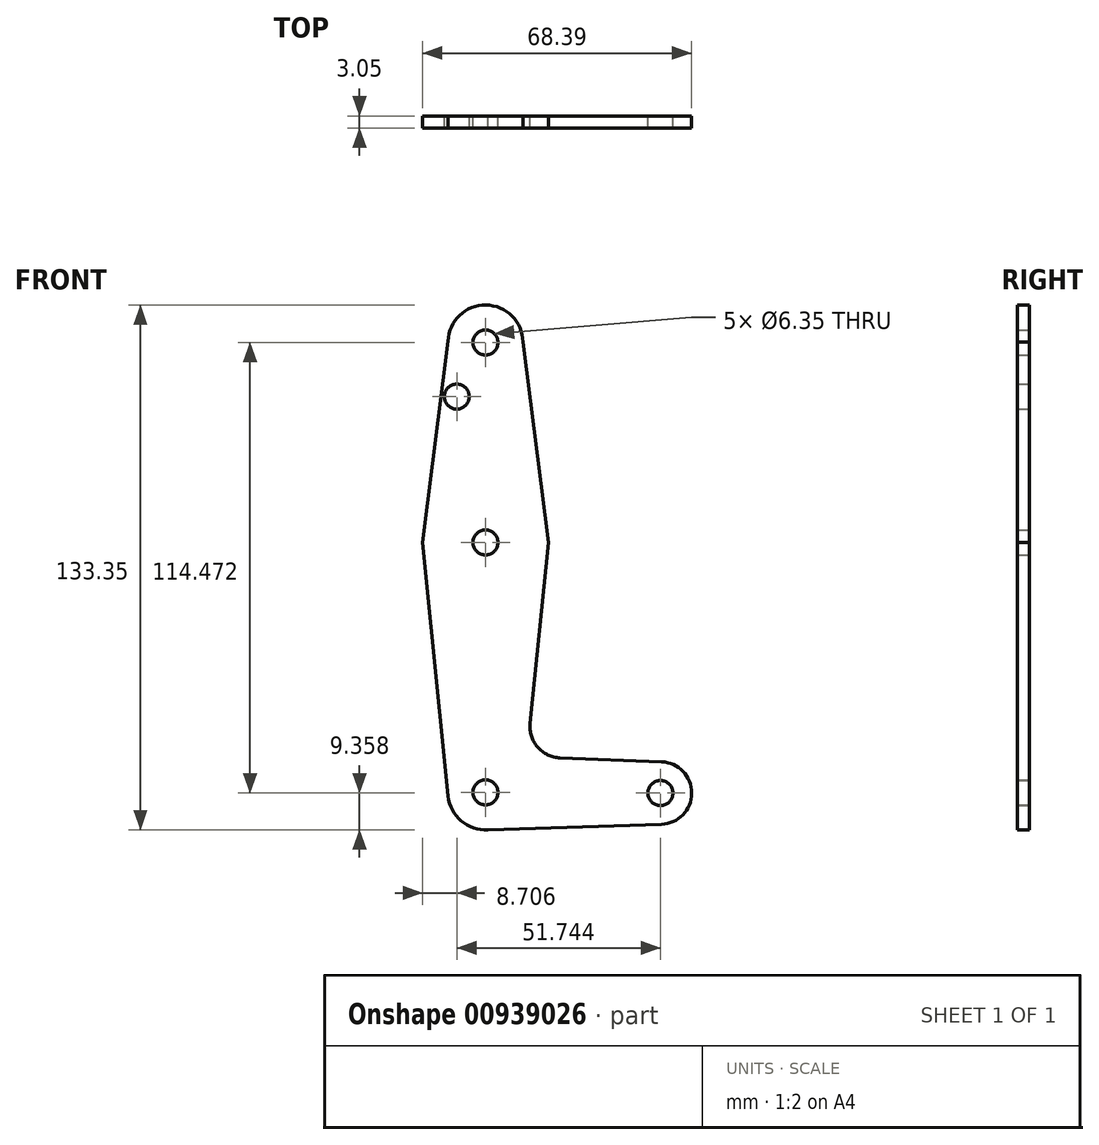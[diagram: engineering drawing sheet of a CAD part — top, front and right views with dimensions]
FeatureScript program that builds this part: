
annotation { "Feature Type Name" : "Feature", "Feature Type Description" : "" }
export const myFeature = defineFeature(function(context is Context, id is Id, definition is map)
    precondition{}
    {
        {
            var Q0;
            Q0=qCreatedBy(makeId("Front.planeOp"),FACE);
            var sketch = newSketch(context, id + "F0", { "sketchPlane" : qUnion([Q0])});
            skCircle(sketch, "E0", {"center": v(0, 0) * mm, "radius": 15.88 * mm});
            skCircle(sketch, "E1", {"center": v(0, 50.8) * mm, "radius": 9.53 * mm});
            skCircle(sketch, "E2", {"center": v(0, -63.5) * mm, "radius": 9.53 * mm});
            skCircle(sketch, "E3", {"center": v(44.45, -63.67) * mm, "radius": 7.94 * mm});
            skLineSegment(sketch, "E4", {"start": v(0, 50.8) * mm, "end": v(0, -63.5) * mm});
            skLineSegment(sketch, "E5", {"start": v(0, -63.5) * mm, "end": v(44.45, -63.67) * mm});
            skLineSegment(sketch, "E6", {"start": v(0, 45.1) * mm, "end": v(0, 50.8) * mm, "construction": true});
            skLineSegment(sketch, "E7", {"start": v(9.52, 50.97) * mm, "end": v(16, 0) * mm});
            skLineSegment(sketch, "E8", {"start": v(-9.52, 51.16) * mm, "end": v(-16, 0) * mm});
            skLineSegment(sketch, "E9", {"start": v(-16, 0) * mm, "end": v(-9.48, -64.46) * mm});
            skLineSegment(sketch, "E10", {"start": v(16, 0) * mm, "end": v(11.35, -45.98) * mm});
            skLineSegment(sketch, "E11", {"start": v(18.94, -54.72) * mm, "end": v(44.76, -55.74) * mm});
            skLineSegment(sketch, "E12", {"start": v(0, -73.03) * mm, "end": v(44.76, -71.6) * mm});
            skCircle(sketch, "E13", {"center": v(0, 50.8) * mm, "radius": 3.18 * mm});
            skCircle(sketch, "E14", {"center": v(0, 0) * mm, "radius": 3.18 * mm});
            skCircle(sketch, "E15", {"center": v(0, -63.5) * mm, "radius": 3.18 * mm});
            skCircle(sketch, "E16", {"center": v(44.45, -63.67) * mm, "radius": 3.18 * mm});
            skCircle(sketch, "E17", {"center": v(-7.3, 37.05) * mm, "radius": 3.18 * mm});
            skArc(sketch, "E18.filletArc", {"start": v(11.35, -45.98) * mm, "mid": v(13.26, -52) * mm, "end": v(18.94, -54.72) * mm});
            skSolve(sketch);
        }
        {
            var Q0;
            Q0 = qSketchRegion(id + "F0", true);
            var Q1;
            {var subQ0=sQuery(id+"F0.wireOp",EDGE,"E4");var subQ1=sQuery(id+"F0.wireOp",EDGE,"E2");var subQ2=makeQuery(id+"F0.imprint","INTERSECT",VERTEX,{"derivedFrom":[subQ1,subQ0]});Q1=makeQuery(id+"F0.imprint","IMPRINT",FACE,{"disambiguationData":[TD([[makeQuery(id+"F0.imprint","IMPRINT",EDGE,{"disambiguationData":[TD([[subQ2,1.0]])],"derivedFrom":subQ1}),1.0]])]});}
            extrude(context, id + "F1", {"entities" : qUnion([Q0, Q1]), "depth" : 3.05 * mm, "offsetDistance" : 25.4 * mm});
        }
    });
